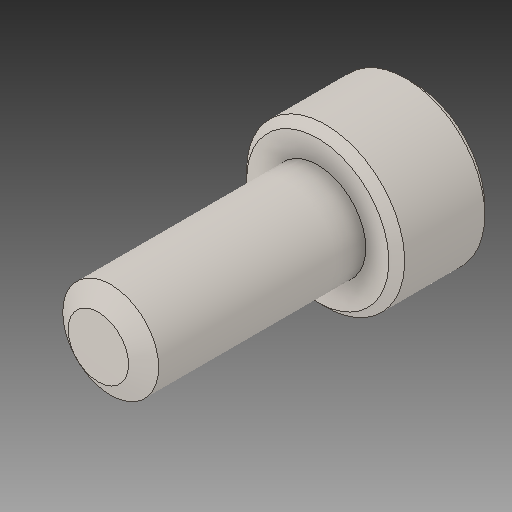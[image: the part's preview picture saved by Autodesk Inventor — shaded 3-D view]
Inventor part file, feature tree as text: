
AUTODESK INVENTOR PART (.ipt)
format: ipt  version: 2018 (Build 220112000, 112)  size: 131,072 bytes
history: native  units: in
note: dims shown in document units (in); Inventor stores cm internally (conversion verified against a paired STEP export)
features: chamfer x1
ambient origin geometry x8: Origin, YZ Plane, XZ Plane, XY Plane, X Axis, Y Axis, Z Axis, Center Point
bodies: Solid1 (feature_tree)
feature tree (1):
  chamfer  "Chamfer1"  [1 undecoded]
note: 1 required parameter value undecoded (feature->parameter linkage not recoverable at this tier; creation-order binding heuristic only, values carry confidence <= 0.55)
